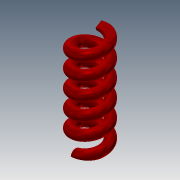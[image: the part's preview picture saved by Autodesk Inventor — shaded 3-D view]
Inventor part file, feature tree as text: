
AUTODESK INVENTOR PART (.ipt)
format: ipt  version: 2015 (Build 190159000, 159)  size: 241,664 bytes
history: native  units: mm
features: sketch x2, extrude x1, helix x1, projected_geometry x1
ambient origin geometry x8: Origin, YZ Plane, XZ Plane, XY Plane, X Axis, Y Axis, Z Axis, Center Point
bodies: Solid1 (feature_tree)
feature tree (5):
  extrude  "Extrusion1"  Depth=84.0mm TaperAngle=0.0deg
  helix  "Coil1"  [1 undecoded]
  sketch  "Sketch1"  dims[d0=45.0mm d1=84.0mm d2=0.0mm d3=84.0mm]
  sketch  "Sketch2"  dims[d4=8.0mm d5=17.0mm d6=18.0mm d7=84.0mm d8=40.0mm d9=0.0mm d10=90.0deg d11=90.0deg d12=0.0mm d13=0.0mm]
  projected_geometry  "Projected Loop1"
note: 1 required parameter value undecoded (feature->parameter linkage not recoverable at this tier; creation-order binding heuristic only, values carry confidence <= 0.55)
